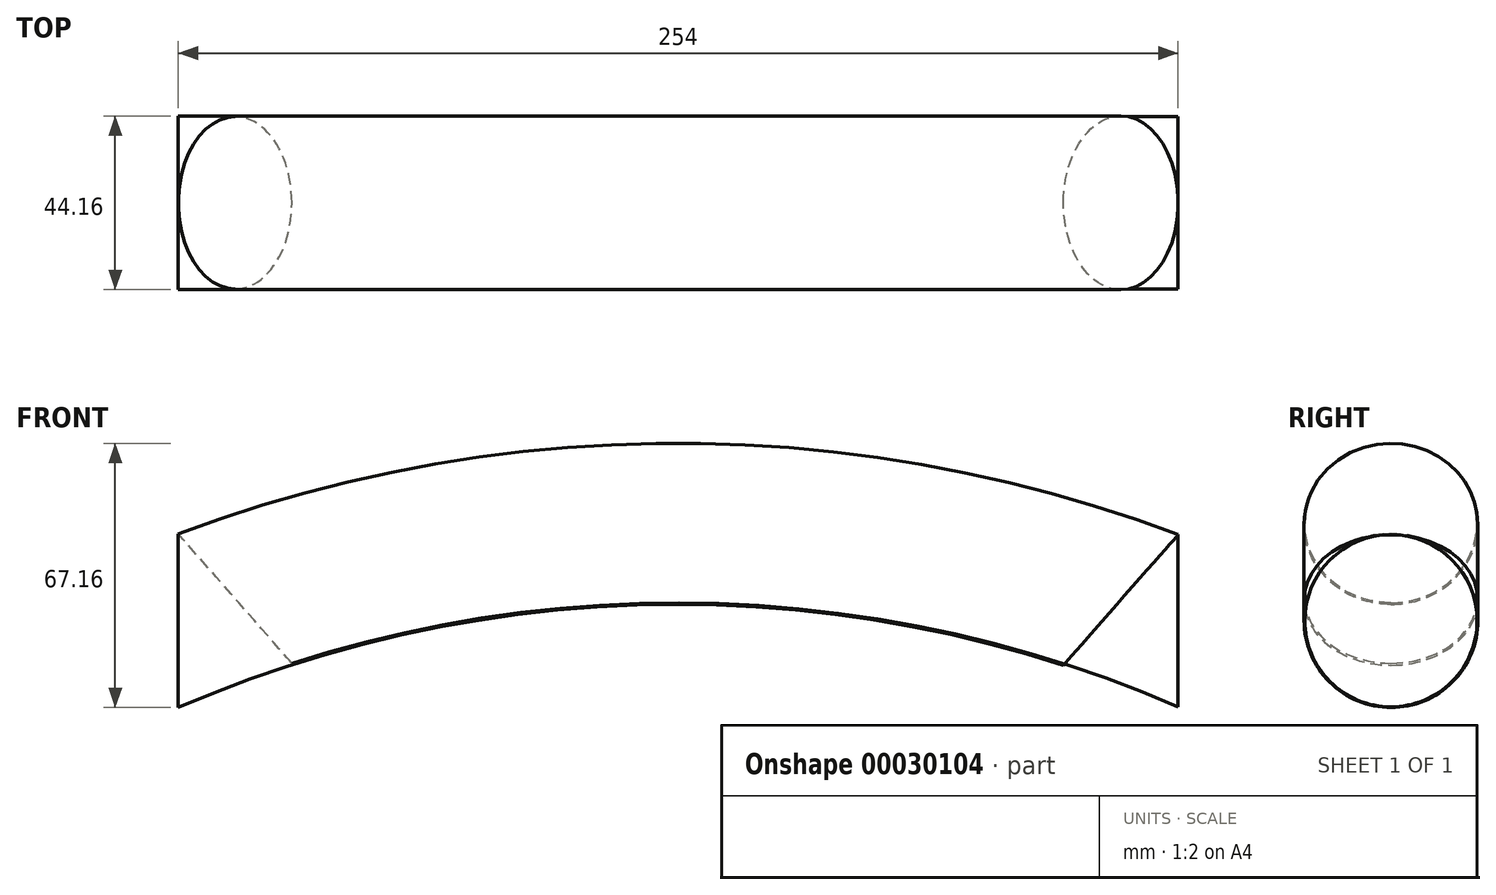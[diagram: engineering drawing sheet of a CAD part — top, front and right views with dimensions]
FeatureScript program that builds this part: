
annotation { "Feature Type Name" : "Feature", "Feature Type Description" : "" }
export const myFeature = defineFeature(function(context is Context, id is Id, definition is map)
    precondition{}
    {
        {
            var Q0;
            Q0=qCreatedBy(makeId("Right.planeOp"),FACE);
            var sketch = newSketch(context, id + "F0", { "sketchPlane" : qUnion([Q0])});
            skCircle(sketch, "E0", {"center": v(0, 0) * mm, "radius": 22.08 * mm});
            skSolve(sketch);
        }
        {
            var Q0;
            Q0=qCreatedBy(makeId("Right.planeOp"),FACE);
            cPlane(context, id + "F1", {"entities" : qUnion([Q0]), "cplaneType" : CPlaneType.OFFSET, "offset" : 127 * mm, "width" : 152.4 * mm, "height" : 152.4 * mm});
        }
        {
            var Q0;
            Q0=qCreatedBy(id+"F1.planeOp",FACE);
            cPlane(context, id + "F2", {"entities" : qUnion([Q0]), "cplaneType" : CPlaneType.OFFSET, "offset" : 127 * mm, "width" : 152.4 * mm, "height" : 152.4 * mm});
        }
        {
            var Q0;
            Q0=qCreatedBy(id+"F1.planeOp",FACE);
            var sketch = newSketch(context, id + "F3", { "sketchPlane" : qUnion([Q0])});
            skCircle(sketch, "E1", {"center": v(-45.2, 27.87) * mm, "radius": 17.22 * mm});
            skSolve(sketch);
        }
        {
            var Q0;
            Q0=qCreatedBy(id+"F2.planeOp",FACE);
            var sketch = newSketch(context, id + "F4", { "sketchPlane" : qUnion([Q0])});
            skCircle(sketch, "E2", {"center": v(0, 0) * mm, "radius": 21.88 * mm});
            skSolve(sketch);
        }
        {
            var Q0;
            Q0=qCreatedBy(makeId("Front.planeOp"),FACE);
            var sketch = newSketch(context, id + "F5", { "sketchPlane" : qUnion([Q0])});
            skLineSegment(sketch, "E3.0", {"start": v(254, 21.88) * mm, "end": v(254, -21.88) * mm});
            skArc(sketch, "E4", {"start": v(254, 21.88) * mm, "mid": v(127.02, 45.08) * mm, "end": v(0, 22.08) * mm});
            skPoint(sketch, "E5.0.end.orphan", {"position": v(0, -22.08) * mm});
            skPoint(sketch, "E6.0.end.orphan", {"position": v(127, 10.65) * mm});
            skPoint(sketch, "E6.0.start.orphan", {"position": v(127, 45.08) * mm});
            skSolve(sketch);
        }
        {
            var Q0;
            Q0=makeQuery(id+"F0.imprint","IMPRINT",FACE,{"disambiguationData":[TD([[makeQuery(id+"F0.imprint","IMPRINT",EDGE,{"derivedFrom":sQuery(id+"F0.wireOp",EDGE,"E0")}),1.0]])]});
            var Q1;
            Q1=makeQuery(id+"F4.imprint","IMPRINT",FACE,{"disambiguationData":[TD([[makeQuery(id+"F4.imprint","IMPRINT",EDGE,{"derivedFrom":sQuery(id+"F4.wireOp",EDGE,"E2")}),1.0]])]});
            var Q2;
            Q2=sQuery(id+"F5.wireOp",EDGE,"E4");
            sweep(context, id + "F6", {"profiles" : qUnion([Q0, Q1]), "path" : qUnion([Q2])});
        }
    });
